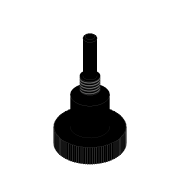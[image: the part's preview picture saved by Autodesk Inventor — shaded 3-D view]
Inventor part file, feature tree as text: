
AUTODESK INVENTOR PART (.ipt)
format: ipt  version: 2022.3 (Build 263350000, 350)  size: 625,664 bytes
history: native  units: mm
features: sketch x8, extrude x5, other x3, plane x2, fillet x2, loft x1, thread x1
ambient origin geometry x8: Origin, YZ Plane, XZ Plane, XY Plane, X Axis, Y Axis, Z Axis, Center Point
bodies: Body1 (feature_tree)
feature tree (22):
  other  "Sólido1"
  extrude  "Extrusión1"  Depth=5.0mm TaperAngle=0.0deg
  extrude  "Extrusión2"  Depth=9.5mm TaperAngle=0.0deg
  sketch  "Boceto3"  dims[d6=-31.8mm d7=3.45mm]
  plane  "Plano de trabajo1"
  extrude  "Extrusión3"  Depth=3.45mm
  plane  "Plano de trabajo2"
  extrude  "Extrusión4"  [1 undecoded]
  sketch  "Boceto6"  dims[d16=0.0mm d17=90.0deg d18=4.0mm d19=0.0mm d20=0.5mm d21=1000.0mm d23=360.0deg]
  sketch  "Boceto7"  dims[d25=5.0mm d26=0.0mm]
  loft  "Solevación1"
  thread  "Rosca1"  [1 undecoded]
  extrude  "Extrusión5"  Depth=0.5mm TaperAngle=0.0deg
  fillet  "Empalme1"  Radius=0.5mm
  fillet  "Empalme2"  Radius=1000.0mm
  sketch  "Boceto1"  dims[d0=17.85mm d1=5.0mm d2=0.0mm]
  sketch  "Boceto2"  dims[d3=9.6mm d4=9.5mm d5=0.0mm]
  sketch  "Boceto4"  dims[d8=20.0mm d9=0.0mm d10=-11.7mm]
  sketch  "Boceto5"  dims[d11=5.0mm d12=4.0mm d13=0.0mm d14=0.0mm d15=90.0deg]
  other  "Aristas1"
  other  "Aristas2"
  sketch  "Boceto8"  dims[d27=0.5mm d28=0.05mm]
note: 2 required parameter values undecoded (feature->parameter linkage not recoverable at this tier; creation-order binding heuristic only, values carry confidence <= 0.55)
